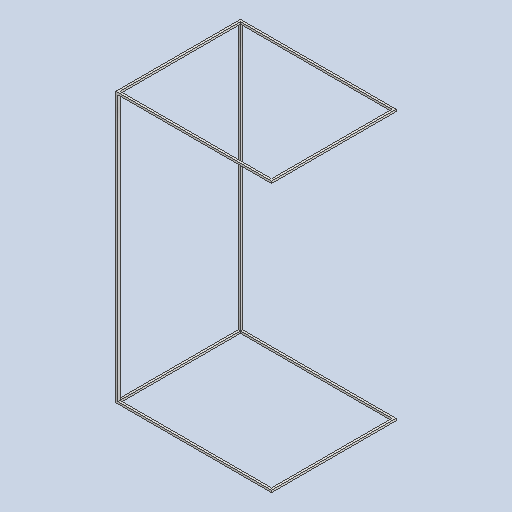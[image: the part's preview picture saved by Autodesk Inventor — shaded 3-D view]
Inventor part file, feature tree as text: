
AUTODESK INVENTOR PART (.ipt)
format: ipt  version: 2023 (Build 270158000, 158)  size: 158,720 bytes
history: native  units: mm
features: projected_geometry x6, extrude x3, sketch x2
ambient origin geometry x8: Origin, YZ Plane, XZ Plane, XY Plane, X Axis, Y Axis, Z Axis, Center Point
bodies: Solid1 (feature_tree)
feature tree (11):
  sketch  "Sketch1"  dims[d0=1500.0mm d1=2600.0mm]
  extrude  "Extrusion1"  Depth=2600.0mm
  extrude  "Extrusion2"  Depth=20.0mm
  extrude  "Extrusion3"  Depth=20.0mm
  sketch  "Sketch2"  dims[d2=20.0mm d3=20.0mm d4=20.0mm d5=20.0mm d6=20.0mm d7=20.0mm d8=20.0mm d9=20.0mm d10=1200.0mm d11=0.0mm d12=20.0mm d13=0.0mm d14=20.0mm d15=0.0mm]
  projected_geometry  "Projected Loop1"
  projected_geometry  "Projected Loop2"
  projected_geometry  "Projected Loop3"
  projected_geometry  "Projected Loop4"
  projected_geometry  "Projected Loop6"
  projected_geometry  "Projected Loop8"
